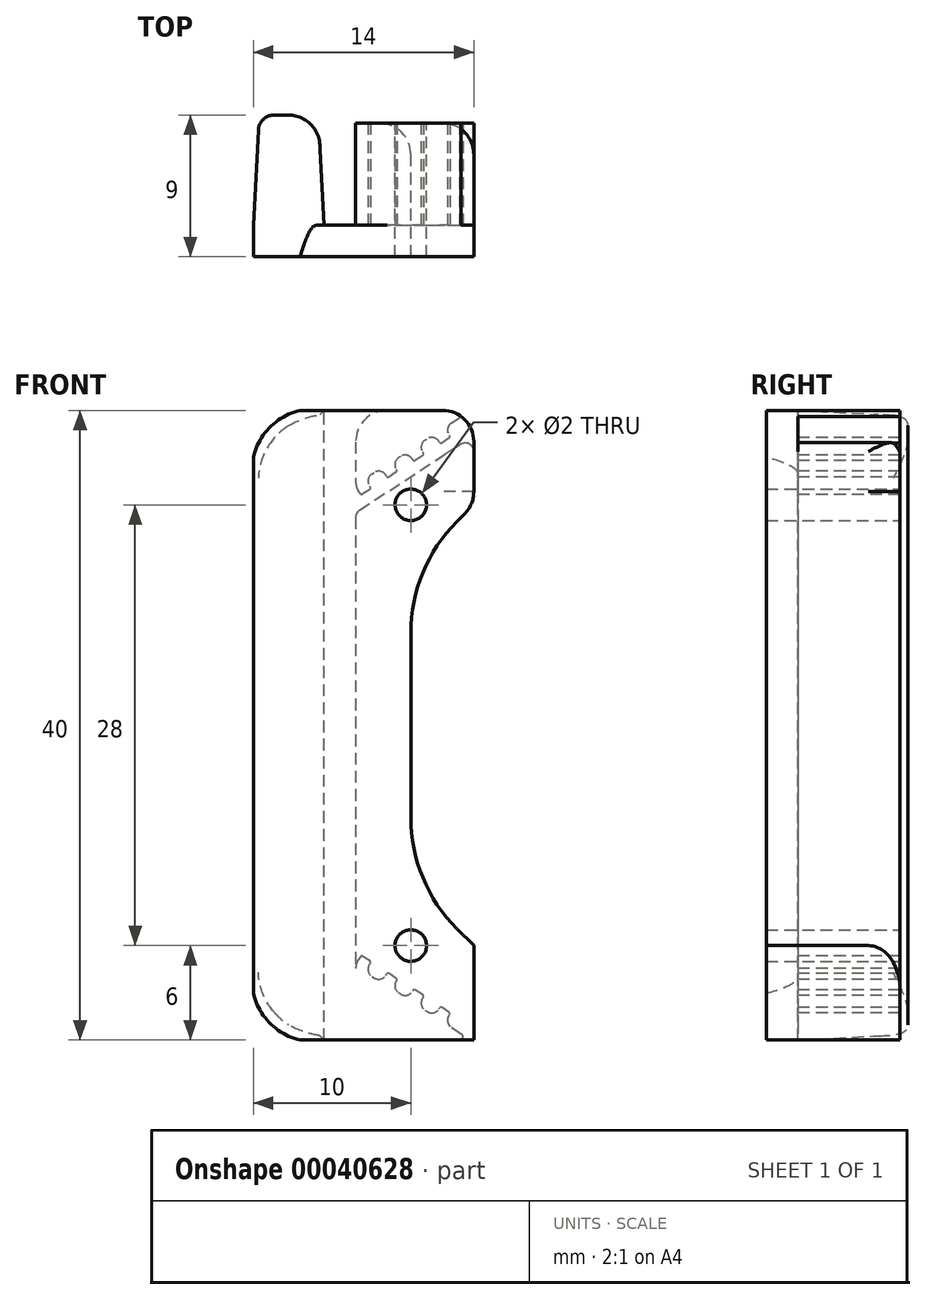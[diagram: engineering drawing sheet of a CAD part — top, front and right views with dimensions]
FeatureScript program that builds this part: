
annotation { "Feature Type Name" : "Feature", "Feature Type Description" : "" }
export const myFeature = defineFeature(function(context is Context, id is Id, definition is map)
    precondition{}
    {
        {
            var Q0;
            Q0=qCreatedBy(makeId("Front.planeOp"),FACE);
            var sketch = newSketch(context, id + "F0", { "sketchPlane" : qUnion([Q0])});
            skLineSegment(sketch, "E0", {"start": v(-0.9, 0) * mm, "end": v(-8, 0) * mm});
            skLineSegment(sketch, "E1", {"start": v(-8, 0) * mm, "end": v(-8, -40) * mm});
            skLineSegment(sketch, "E2", {"start": v(-8, -40) * mm, "end": v(0, -40) * mm});
            skLineSegment(sketch, "E3", {"start": v(0, -40) * mm, "end": v(0, -37.4) * mm});
            skLineSegment(sketch, "E4", {"start": v(-7.5, 0) * mm, "end": v(-7.5, -4.54) * mm});
            skLineSegment(sketch, "E5", {"start": v(-7.25, -6.34) * mm, "end": v(-0.85, -2.15) * mm});
            skLineSegment(sketch, "E6.0", {"start": v(-8.05, -5.67) * mm, "end": v(-0.55, -0.75) * mm, "construction": true});
            skLineSegment(sketch, "E7.0", {"start": v(-6.47, -4.04) * mm, "end": v(-6.35, -3.95) * mm});
            skLineSegment(sketch, "E8", {"start": v(-6.1, -5.6) * mm, "end": v(-6.93, -4.34) * mm, "construction": true});
            skLineSegment(sketch, "E9.0", {"start": v(-4.68, -4.12) * mm, "end": v(-5.01, -3.62) * mm, "construction": true});
            skLineSegment(sketch, "E10.0", {"start": v(-2.52, -3.78) * mm, "end": v(-3.34, -2.52) * mm, "construction": true});
            skLineSegment(sketch, "E11.0", {"start": v(-0.84, -2.68) * mm, "end": v(-1.67, -1.43) * mm, "construction": true});
            skLineSegment(sketch, "E12", {"start": v(-6.63, -4.8) * mm, "end": v(-6.58, -4.88) * mm});
            skLineSegment(sketch, "E13", {"start": v(-6.6, -5.02) * mm, "end": v(-7.06, -5.32) * mm});
            skLineSegment(sketch, "E14", {"start": v(-7.2, -5.3) * mm, "end": v(-7.34, -5.09) * mm});
            skLineSegment(sketch, "E15", {"start": v(-4.92, -3.75) * mm, "end": v(-4.9, -3.78) * mm});
            skLineSegment(sketch, "E16", {"start": v(-4.93, -3.92) * mm, "end": v(-5.4, -4.22) * mm});
            skLineSegment(sketch, "E17", {"start": v(-5.53, -4.2) * mm, "end": v(-5.58, -4.11) * mm});
            skPoint(sketch, "E18.newPointA", {"position": v(-6.93, -4.34) * mm});
            skArc(sketch, "E18.filletArc", {"start": v(-6.47, -4.04) * mm, "mid": v(-6.7, -4.38) * mm, "end": v(-6.63, -4.8) * mm});
            skLineSegment(sketch, "E19", {"start": v(-3.25, -2.66) * mm, "end": v(-3.2, -2.72) * mm});
            skLineSegment(sketch, "E20", {"start": v(-3.24, -2.86) * mm, "end": v(-3.73, -3.18) * mm});
            skLineSegment(sketch, "E21", {"start": v(-3.86, -3.15) * mm, "end": v(-3.9, -3.09) * mm});
            skLineSegment(sketch, "E22", {"start": v(-4.67, -2.93) * mm, "end": v(-4.77, -3) * mm});
            skArc(sketch, "E23.filletArc", {"start": v(-4.77, -3) * mm, "mid": v(-5, -3.34) * mm, "end": v(-4.92, -3.75) * mm});
            skPoint(sketch, "E24.visualSharp", {"position": v(-4.2, -2.63) * mm});
            skArc(sketch, "E24.filletArc", {"start": v(-3.9, -3.09) * mm, "mid": v(-4.25, -2.85) * mm, "end": v(-4.67, -2.93) * mm});
            skArc(sketch, "E25.filletArc", {"start": v(-5.58, -4.11) * mm, "mid": v(-5.93, -3.88) * mm, "end": v(-6.35, -3.95) * mm});
            skLineSegment(sketch, "E26", {"start": v(-7.5, -6.8) * mm, "end": v(-7.5, -33.2) * mm});
            skPoint(sketch, "E27.visualSharp", {"position": v(-7.5, -6.5) * mm});
            skArc(sketch, "E27.filletArc", {"start": v(-7.25, -6.34) * mm, "mid": v(-7.43, -6.54) * mm, "end": v(-7.5, -6.8) * mm});
            skPoint(sketch, "E28.visualSharp", {"position": v(-7.5, -4.84) * mm});
            skArc(sketch, "E28.filletArc", {"start": v(-7.5, -4.54) * mm, "mid": v(-7.46, -4.83) * mm, "end": v(-7.34, -5.09) * mm});
            skLineSegment(sketch, "E29", {"start": v(-1.58, -1.56) * mm, "end": v(-1.54, -1.62) * mm});
            skLineSegment(sketch, "E30", {"start": v(-1.57, -1.76) * mm, "end": v(-2.03, -2.06) * mm});
            skLineSegment(sketch, "E31", {"start": v(-2.16, -2.03) * mm, "end": v(-2.2, -1.97) * mm});
            skLineSegment(sketch, "E32", {"start": v(-3.1, -1.9) * mm, "end": v(-2.97, -1.81) * mm});
            skArc(sketch, "E33.filletArc", {"start": v(-3.1, -1.9) * mm, "mid": v(-3.33, -2.24) * mm, "end": v(-3.25, -2.66) * mm});
            skArc(sketch, "E34.filletArc", {"start": v(-2.2, -1.97) * mm, "mid": v(-2.55, -1.73) * mm, "end": v(-2.97, -1.81) * mm});
            skCircle(sketch, "E35", {"center": v(-4, -6) * mm, "radius": 1 * mm});
            skLineSegment(sketch, "E36", {"start": v(-1.42, -0.8) * mm, "end": v(-0.78, -0.38) * mm});
            skArc(sketch, "E37.filletArc", {"start": v(-1.42, -0.8) * mm, "mid": v(-1.66, -1.15) * mm, "end": v(-1.58, -1.56) * mm});
            skPoint(sketch, "E38.newPointB", {"position": v(0, 0) * mm});
            skArc(sketch, "E38.filletArc", {"start": v(0, -2.6) * mm, "mid": v(-0.29, -2.12) * mm, "end": v(-0.85, -2.15) * mm});
            skLineSegment(sketch, "E39", {"start": v(0, -2.6) * mm, "end": v(0, 0) * mm});
            skArc(sketch, "E40.filletArc", {"start": v(-0.78, -0.38) * mm, "mid": v(-0.7, -0.15) * mm, "end": v(-0.9, 0) * mm});
            skLineSegment(sketch, "E41", {"start": v(-0.9, 0) * mm, "end": v(0, 0) * mm});
            skPoint(sketch, "E42.visualSharp", {"position": v(-4.85, -3.87) * mm});
            skArc(sketch, "E42.filletArc", {"start": v(-4.93, -3.92) * mm, "mid": v(-4.89, -3.86) * mm, "end": v(-4.9, -3.78) * mm});
            skPoint(sketch, "E43.visualSharp", {"position": v(-5.48, -4.28) * mm});
            skArc(sketch, "E43.filletArc", {"start": v(-5.53, -4.2) * mm, "mid": v(-5.47, -4.24) * mm, "end": v(-5.4, -4.22) * mm});
            skPoint(sketch, "E44.visualSharp", {"position": v(-6.52, -4.96) * mm});
            skArc(sketch, "E44.filletArc", {"start": v(-6.6, -5.02) * mm, "mid": v(-6.56, -4.96) * mm, "end": v(-6.58, -4.88) * mm});
            skPoint(sketch, "E45.visualSharp", {"position": v(-7.15, -5.38) * mm});
            skArc(sketch, "E45.filletArc", {"start": v(-7.2, -5.3) * mm, "mid": v(-7.14, -5.34) * mm, "end": v(-7.06, -5.32) * mm});
            skPoint(sketch, "E46.visualSharp", {"position": v(-3.8, -3.24) * mm});
            skArc(sketch, "E46.filletArc", {"start": v(-3.86, -3.15) * mm, "mid": v(-3.8, -3.2) * mm, "end": v(-3.73, -3.18) * mm});
            skPoint(sketch, "E47.visualSharp", {"position": v(-3.15, -2.8) * mm});
            skArc(sketch, "E47.filletArc", {"start": v(-3.24, -2.86) * mm, "mid": v(-3.2, -2.8) * mm, "end": v(-3.2, -2.72) * mm});
            skPoint(sketch, "E48.visualSharp", {"position": v(-2.1, -2.12) * mm});
            skArc(sketch, "E48.filletArc", {"start": v(-2.16, -2.03) * mm, "mid": v(-2.1, -2.08) * mm, "end": v(-2.03, -2.06) * mm});
            skPoint(sketch, "E49.visualSharp", {"position": v(-1.48, -1.7) * mm});
            skArc(sketch, "E49.filletArc", {"start": v(-1.57, -1.76) * mm, "mid": v(-1.52, -1.7) * mm, "end": v(-1.54, -1.62) * mm});
            skLineSegment(sketch, "E50", {"start": v(-8, -20) * mm, "end": v(0, -20) * mm, "construction": true});
            skArc(sketch, "E51.MirrorCS", {"start": v(-3.86, -36.85) * mm, "mid": v(-3.8, -36.8) * mm, "end": v(-3.73, -36.82) * mm});
            skLineSegment(sketch, "E52.MirrorCS", {"start": v(-3.86, -36.85) * mm, "end": v(-3.9, -36.91) * mm});
            skArc(sketch, "E53.MirrorCS", {"start": v(-3.9, -36.91) * mm, "mid": v(-4.25, -37.15) * mm, "end": v(-4.67, -37.07) * mm});
            skLineSegment(sketch, "E54.MirrorCS", {"start": v(-4.93, -36.08) * mm, "end": v(-5.4, -35.78) * mm});
            skArc(sketch, "E55.MirrorCS", {"start": v(-4.93, -36.08) * mm, "mid": v(-4.89, -36.14) * mm, "end": v(-4.9, -36.22) * mm});
            skLineSegment(sketch, "E56.MirrorCS", {"start": v(-4.68, -35.88) * mm, "end": v(-5.01, -36.38) * mm, "construction": true});
            skLineSegment(sketch, "E57.MirrorCS", {"start": v(-3.24, -37.14) * mm, "end": v(-3.73, -36.82) * mm});
            skLineSegment(sketch, "E58.MirrorCS", {"start": v(-3.25, -37.34) * mm, "end": v(-3.2, -37.28) * mm});
            skArc(sketch, "E59.MirrorCS", {"start": v(-5.53, -35.8) * mm, "mid": v(-5.47, -35.76) * mm, "end": v(-5.4, -35.78) * mm});
            skArc(sketch, "E60.MirrorCS", {"start": v(-5.58, -35.89) * mm, "mid": v(-5.93, -36.12) * mm, "end": v(-6.35, -36.05) * mm});
            skLineSegment(sketch, "E61.MirrorCS", {"start": v(-6.63, -35.2) * mm, "end": v(-6.58, -35.12) * mm});
            skArc(sketch, "E62.MirrorCS", {"start": v(-6.6, -34.98) * mm, "mid": v(-6.56, -35.04) * mm, "end": v(-6.58, -35.12) * mm});
            skLineSegment(sketch, "E63.MirrorCS", {"start": v(-1.58, -38.44) * mm, "end": v(-1.54, -38.38) * mm});
            skLineSegment(sketch, "E64.MirrorCS", {"start": v(-7.2, -34.7) * mm, "end": v(-7.34, -34.91) * mm});
            skLineSegment(sketch, "E65.MirrorCS", {"start": v(-6.6, -34.98) * mm, "end": v(-7.06, -34.68) * mm});
            skLineSegment(sketch, "E66.MirrorCS", {"start": v(-6.1, -34.4) * mm, "end": v(-6.93, -35.66) * mm, "construction": true});
            skArc(sketch, "E67.MirrorCS", {"start": v(-3.1, -38.1) * mm, "mid": v(-3.33, -37.76) * mm, "end": v(-3.25, -37.34) * mm});
            skArc(sketch, "E68.MirrorCS", {"start": v(-1.57, -38.24) * mm, "mid": v(-1.52, -38.3) * mm, "end": v(-1.54, -38.38) * mm});
            skLineSegment(sketch, "E69.MirrorCS", {"start": v(-1.57, -38.24) * mm, "end": v(-2.03, -37.94) * mm});
            skArc(sketch, "E70.MirrorCS", {"start": v(-1.42, -39.2) * mm, "mid": v(-1.66, -38.85) * mm, "end": v(-1.58, -38.44) * mm});
            skArc(sketch, "E71.MirrorCS", {"start": v(-2.2, -38.03) * mm, "mid": v(-2.55, -38.27) * mm, "end": v(-2.97, -38.19) * mm});
            skArc(sketch, "E72.MirrorCS", {"start": v(-7.5, -35.46) * mm, "mid": v(-7.46, -35.17) * mm, "end": v(-7.34, -34.91) * mm});
            skLineSegment(sketch, "E73.MirrorCS", {"start": v(-3.1, -38.1) * mm, "end": v(-2.97, -38.19) * mm});
            skArc(sketch, "E74.MirrorCS", {"start": v(-6.47, -35.96) * mm, "mid": v(-6.7, -35.62) * mm, "end": v(-6.63, -35.2) * mm});
            skLineSegment(sketch, "E75.MirrorCS", {"start": v(-4.67, -37.07) * mm, "end": v(-4.77, -37) * mm});
            skArc(sketch, "E76.MirrorCS", {"start": v(-4.77, -37) * mm, "mid": v(-5, -36.66) * mm, "end": v(-4.92, -36.25) * mm});
            skLineSegment(sketch, "E77.MirrorCS", {"start": v(-0.9, -40) * mm, "end": v(0, -40) * mm});
            skArc(sketch, "E78.MirrorCS", {"start": v(-0.78, -39.62) * mm, "mid": v(-0.7, -39.85) * mm, "end": v(-0.9, -40) * mm});
            skArc(sketch, "E79.MirrorCS", {"start": v(0, -37.4) * mm, "mid": v(-0.29, -37.88) * mm, "end": v(-0.85, -37.85) * mm});
            skLineSegment(sketch, "E80.MirrorCS", {"start": v(-1.42, -39.2) * mm, "end": v(-0.78, -39.62) * mm});
            skArc(sketch, "E81.MirrorCS", {"start": v(-7.25, -33.66) * mm, "mid": v(-7.43, -33.46) * mm, "end": v(-7.5, -33.2) * mm});
            skLineSegment(sketch, "E82.MirrorCS", {"start": v(-8.05, -34.33) * mm, "end": v(-0.55, -39.25) * mm, "construction": true});
            skLineSegment(sketch, "E83.MirrorCS", {"start": v(-2.52, -36.22) * mm, "end": v(-3.34, -37.48) * mm, "construction": true});
            skLineSegment(sketch, "E84.MirrorCS", {"start": v(-0.84, -37.32) * mm, "end": v(-1.67, -38.57) * mm, "construction": true});
            skPoint(sketch, "E85.MirrorP", {"position": v(-4.2, -37.37) * mm});
            skPoint(sketch, "E86.MirrorP", {"position": v(-3.15, -37.2) * mm});
            skPoint(sketch, "E87.MirrorP", {"position": v(-4.85, -36.13) * mm});
            skPoint(sketch, "E88.MirrorP", {"position": v(-5.48, -35.72) * mm});
            skPoint(sketch, "E89.MirrorP", {"position": v(-6.93, -35.66) * mm});
            skPoint(sketch, "E90.MirrorP", {"position": v(-3.8, -36.76) * mm});
            skLineSegment(sketch, "E91.MirrorCS", {"start": v(-7.25, -33.66) * mm, "end": v(-0.85, -37.85) * mm});
            skPoint(sketch, "E92.MirrorP", {"position": v(-7.5, -35.16) * mm});
            skPoint(sketch, "E93.MirrorP", {"position": v(-1.48, -38.3) * mm});
            skPoint(sketch, "E94.MirrorP", {"position": v(-6.52, -35.04) * mm});
            skPoint(sketch, "E95.MirrorP", {"position": v(-2.1, -37.88) * mm});
            skLineSegment(sketch, "E96.MirrorCS", {"start": v(0, -37.4) * mm, "end": v(0, -40) * mm});
            skPoint(sketch, "E97.MirrorP", {"position": v(-7.5, -33.5) * mm});
            skPoint(sketch, "E98.MirrorP", {"position": v(-7.15, -34.62) * mm});
            skPoint(sketch, "E99.MirrorP", {"position": v(0, -40) * mm});
            skLineSegment(sketch, "E100.MirrorCS", {"start": v(-0.9, -40) * mm, "end": v(-0.9, -40) * mm});
            skCircle(sketch, "E101.MirrorC", {"center": v(-4, -34) * mm, "radius": 1 * mm});
            skLineSegment(sketch, "E102.MirrorCS", {"start": v(-7.5, -40) * mm, "end": v(-7.5, -35.46) * mm});
            skPoint(sketch, "E103.newPointA", {"position": v(-7.2, -34.7) * mm});
            skPoint(sketch, "E103.newPointB", {"position": v(-7.06, -34.68) * mm});
            skArc(sketch, "E103.filletArc", {"start": v(-7.06, -34.68) * mm, "mid": v(-7.14, -34.66) * mm, "end": v(-7.2, -34.7) * mm});
            skPoint(sketch, "E104.newPointA", {"position": v(-3.2, -37.28) * mm});
            skPoint(sketch, "E104.newPointB", {"position": v(-3.24, -37.14) * mm});
            skArc(sketch, "E104.filletArc", {"start": v(-3.2, -37.28) * mm, "mid": v(-3.2, -37.2) * mm, "end": v(-3.24, -37.14) * mm});
            skLineSegment(sketch, "E105", {"start": v(-2.2, -38.03) * mm, "end": v(-2.16, -37.97) * mm});
            skPoint(sketch, "E106.newPointA", {"position": v(-2.03, -37.94) * mm});
            skArc(sketch, "E106.filletArc", {"start": v(-2.03, -37.94) * mm, "mid": v(-2.1, -37.92) * mm, "end": v(-2.16, -37.97) * mm});
            skLineSegment(sketch, "E107", {"start": v(-5.58, -35.89) * mm, "end": v(-5.53, -35.8) * mm});
            skLineSegment(sketch, "E108", {"start": v(-6.47, -35.96) * mm, "end": v(-6.35, -36.05) * mm});
            skLineSegment(sketch, "E109", {"start": v(-7.5, -33.2) * mm, "end": v(-7.5, -35.46) * mm});
            skLineSegment(sketch, "E110", {"start": v(-7.5, -35.46) * mm, "end": v(-7.5, -40) * mm});
            skLineSegment(sketch, "E111", {"start": v(-0.9, -40) * mm, "end": v(-8, -40) * mm});
            skLineSegment(sketch, "E112", {"start": v(0, -37.4) * mm, "end": v(0, -2.6) * mm});
            skLineSegment(sketch, "E113", {"start": v(-4.92, -36.25) * mm, "end": v(-4.9, -36.22) * mm});
            skLineSegment(sketch, "E114", {"start": v(-8, 0) * mm, "end": v(-14, 0) * mm});
            skLineSegment(sketch, "E115", {"start": v(-14, 0) * mm, "end": v(-14, -40) * mm});
            skLineSegment(sketch, "E116", {"start": v(-14, -40) * mm, "end": v(-8, -40) * mm});
            skLineSegment(sketch, "E117", {"start": v(-9.5, 0) * mm, "end": v(-9.5, -40) * mm});
            skLineSegment(sketch, "E118", {"start": v(0, -6) * mm, "end": v(-4, -10) * mm});
            skLineSegment(sketch, "E119", {"start": v(-4, -10) * mm, "end": v(-4, -30) * mm});
            skLineSegment(sketch, "E120", {"start": v(-4, -30) * mm, "end": v(0, -34) * mm});
            skSolve(sketch);
        }
        {
            var Q0;
            Q0=makeQuery(id+"F0.imprint","IMPRINT",FACE,{"disambiguationData":[TD([[makeQuery(id+"F0.imprint","IMPRINT",EDGE,{"derivedFrom":sQuery(id+"F0.wireOp",EDGE,"E5")}),-1.0]])]});
            var Q1;
            Q1=makeQuery(id+"F0.imprint","IMPRINT",FACE,{"disambiguationData":[TD([[makeQuery(id+"F0.imprint","IMPRINT",EDGE,{"derivedFrom":sQuery(id+"F0.wireOp",EDGE,"E51.MirrorCS")}),-1.0]])]});
            var Q2;
            {var subQ2=sQuery(id+"F0.wireOp",EDGE,"E4");Q2=makeQuery(id+"F0.imprint","IMPRINT",FACE,{"disambiguationData":[TD([[makeQuery(id+"F0.imprint","IMPRINT",EDGE,{"derivedFrom":subQ2}),1.0]])]});}
            var Q3;
            Q3=makeQuery(id+"F0.imprint","IMPRINT",FACE,{"disambiguationData":[TD([[makeQuery(id+"F0.imprint","IMPRINT",EDGE,{"derivedFrom":sQuery(id+"F0.wireOp",EDGE,"E51.MirrorCS")}),1.0]])]});
            var Q4;
            {var subQ2=sQuery(id+"F0.wireOp",EDGE,"E1");Q4=makeQuery(id+"F0.imprint","IMPRINT",FACE,{"disambiguationData":[TD([[makeQuery(id+"F0.imprint","IMPRINT",EDGE,{"derivedFrom":subQ2}),1.0]])]});}
            var Q5;
            {var subQ2=sQuery(id+"F0.wireOp",EDGE,"E1");Q5=makeQuery(id+"F0.imprint","IMPRINT",FACE,{"disambiguationData":[TD([[makeQuery(id+"F0.imprint","IMPRINT",EDGE,{"derivedFrom":subQ2}),-1.0]])]});}
            var Q6;
            {var subQ2=sQuery(id+"F0.wireOp",EDGE,"E115");Q6=makeQuery(id+"F0.imprint","IMPRINT",FACE,{"disambiguationData":[TD([[makeQuery(id+"F0.imprint","IMPRINT",EDGE,{"derivedFrom":subQ2}),1.0]])]});}
            extrude(context, id + "F1", {"entities" : qUnion([Q0, Q1, Q2, Q3, Q4, Q5, Q6]), "depth" : 2 * mm});
        }
        {
            var Q0;
            Q0=makeQuery(id+"F0.imprint","IMPRINT",FACE,{"disambiguationData":[TD([[makeQuery(id+"F0.imprint","IMPRINT",EDGE,{"derivedFrom":sQuery(id+"F0.wireOp",EDGE,"E51.MirrorCS")}),-1.0]])]});
            var Q1;
            Q1=makeQuery(id+"F0.imprint","IMPRINT",FACE,{"disambiguationData":[TD([[makeQuery(id+"F0.imprint","IMPRINT",EDGE,{"derivedFrom":sQuery(id+"F0.wireOp",EDGE,"E5")}),-1.0]])]});
            var Q2;
            {var subQ2=sQuery(id+"F0.wireOp",EDGE,"E4");Q2=makeQuery(id+"F0.imprint","IMPRINT",FACE,{"disambiguationData":[TD([[makeQuery(id+"F0.imprint","IMPRINT",EDGE,{"derivedFrom":subQ2}),1.0]])]});}
            extrude(context, id + "F2", {"entities" : qUnion([Q0, Q1, Q2]), "operationType" : NewBodyOperationType.ADD, "oppositeDirection" : true, "depth" : 6.5 * mm});
        }
        {
            var Q0;
            {var subQ2=sQuery(id+"F0.wireOp",EDGE,"E115");Q0=makeQuery(id+"F0.imprint","IMPRINT",FACE,{"disambiguationData":[TD([[makeQuery(id+"F0.imprint","IMPRINT",EDGE,{"derivedFrom":subQ2}),1.0]])]});}
            extrude(context, id + "F3", {"entities" : qUnion([Q0]), "operationType" : NewBodyOperationType.ADD, "oppositeDirection" : true, "depth" : 7 * mm, "hasDraft" : true, "draftAngle" : 3 * degree, "draftPullDirection" : true});
        }
        {
            var Q0;
            Q0=makeQuery(id+"F3.opExtrude","CAP_EDGE",EDGE,{"disambiguationData":[OSD([sQuery(id+"F0.wireOp",EDGE,"E117")])],"isStart":false});
            fillet(context, id + "F4", {"entities" : qUnion([Q0]), "radius" : 2 * mm, "allowEdgeOverflow" : false});
        }
        {
            var Q0;
            Q0=makeQuery(id+"F3.opExtrude","SWEPT_EDGE",EDGE,{"disambiguationData":[OSD([sQuery(id+"F0.wireOp",EDGE,"E114"),sQuery(id+"F0.wireOp",EDGE,"E115")])]});
            var Q1;
            Q1=makeQuery(id+"F3.opExtrude","SWEPT_EDGE",EDGE,{"disambiguationData":[OSD([sQuery(id+"F0.wireOp",EDGE,"E115"),sQuery(id+"F0.wireOp",EDGE,"E116")])]});
            fillet(context, id + "F5", {"entities" : qUnion([Q0, Q1]), "radius" : 4 * mm, "tangentPropagation" : true, "allowEdgeOverflow" : false});
        }
        {
            var Q0;
            Q0=makeQuery(id+"F1.opExtrude","SWEPT_EDGE",EDGE,{"disambiguationData":[OSD([sQuery(id+"F0.wireOp",EDGE,"E77.MirrorCS"),sQuery(id+"F0.wireOp",EDGE,"E96.MirrorCS")])]});
            var Q1;
            Q1=makeQuery(id+"F1.opExtrude","SWEPT_EDGE",EDGE,{"disambiguationData":[OSD([sQuery(id+"F0.wireOp",EDGE,"E39"),sQuery(id+"F0.wireOp",EDGE,"E41")])]});
            var Q2;
            Q2=makeQuery(id+"F2.opExtrude","CAP_EDGE",EDGE,{"disambiguationData":[OSD([sQuery(id+"F0.wireOp",EDGE,"E112")])],"isStart":false});
            var Q3;
            Q3=makeQuery(id+"F2.opExtrude","SWEPT_EDGE",EDGE,{"disambiguationData":[OSD([sQuery(id+"F0.wireOp",EDGE,"E110"),sQuery(id+"F0.wireOp",EDGE,"E111")])]});
            var Q4;
            Q4=makeQuery(id+"F2.opExtrude","SWEPT_EDGE",EDGE,{"disambiguationData":[OSD([sQuery(id+"F0.wireOp",EDGE,"E0"),sQuery(id+"F0.wireOp",EDGE,"E4")])]});
            fillet(context, id + "F6", {"entities" : qUnion([Q0, Q1, Q2, Q3, Q4]), "radius" : 2 * mm, "allowEdgeOverflow" : false});
        }
        {
            var Q0;
            {var subQ0=sQuery(id+"F0.wireOp",EDGE,"E118");var subQ1=sQuery(id+"F0.wireOp",EDGE,"E119");Q0=makeQuery(id+"F2.boolean.opBoolean","MERGE",EDGE,{"derivedFrom":[makeQuery(id+"F1.opExtrude","SWEPT_EDGE",EDGE,{"disambiguationData":[OSD([subQ0,subQ1])]}),makeQuery(id+"F2.opExtrude","SWEPT_EDGE",EDGE,{"disambiguationData":[OSD([subQ0,subQ1])]})]});}
            var Q1;
            {var subQ0=sQuery(id+"F0.wireOp",EDGE,"E119");var subQ1=sQuery(id+"F0.wireOp",EDGE,"E120");Q1=makeQuery(id+"F2.boolean.opBoolean","MERGE",EDGE,{"derivedFrom":[makeQuery(id+"F1.opExtrude","SWEPT_EDGE",EDGE,{"disambiguationData":[OSD([subQ0,subQ1])]}),makeQuery(id+"F2.opExtrude","SWEPT_EDGE",EDGE,{"disambiguationData":[OSD([subQ0,subQ1])]})]});}
            fillet(context, id + "F7", {"entities" : qUnion([Q0, Q1]), "radius" : 10 * mm, "tangentPropagation" : true, "allowEdgeOverflow" : false});
        }
        {
            var Q0;
            {var subQ0=sQuery(id+"F0.wireOp",EDGE,"E112");var subQ1=sQuery(id+"F0.wireOp",EDGE,"E118");Q0=makeQuery(id+"F2.boolean.opBoolean","MERGE",EDGE,{"derivedFrom":[makeQuery(id+"F1.opExtrude","SWEPT_EDGE",EDGE,{"disambiguationData":[OSD([subQ0,subQ1])]}),makeQuery(id+"F2.opExtrude","SWEPT_EDGE",EDGE,{"disambiguationData":[OSD([subQ0,subQ1])]})]});}
            fillet(context, id + "F8", {"entities" : qUnion([Q0]), "radius" : 2 * mm, "tangentPropagation" : true, "allowEdgeOverflow" : false});
        }
        {
            var Q0;
            Q0=makeQuery(id+"F3.opExtrude","CAP_EDGE",EDGE,{"disambiguationData":[OSD([sQuery(id+"F0.wireOp",EDGE,"E115")])],"isStart":false});
            fillet(context, id + "F9", {"entities" : qUnion([Q0]), "radius" : 1 * mm, "allowEdgeOverflow" : false});
        }
    });
